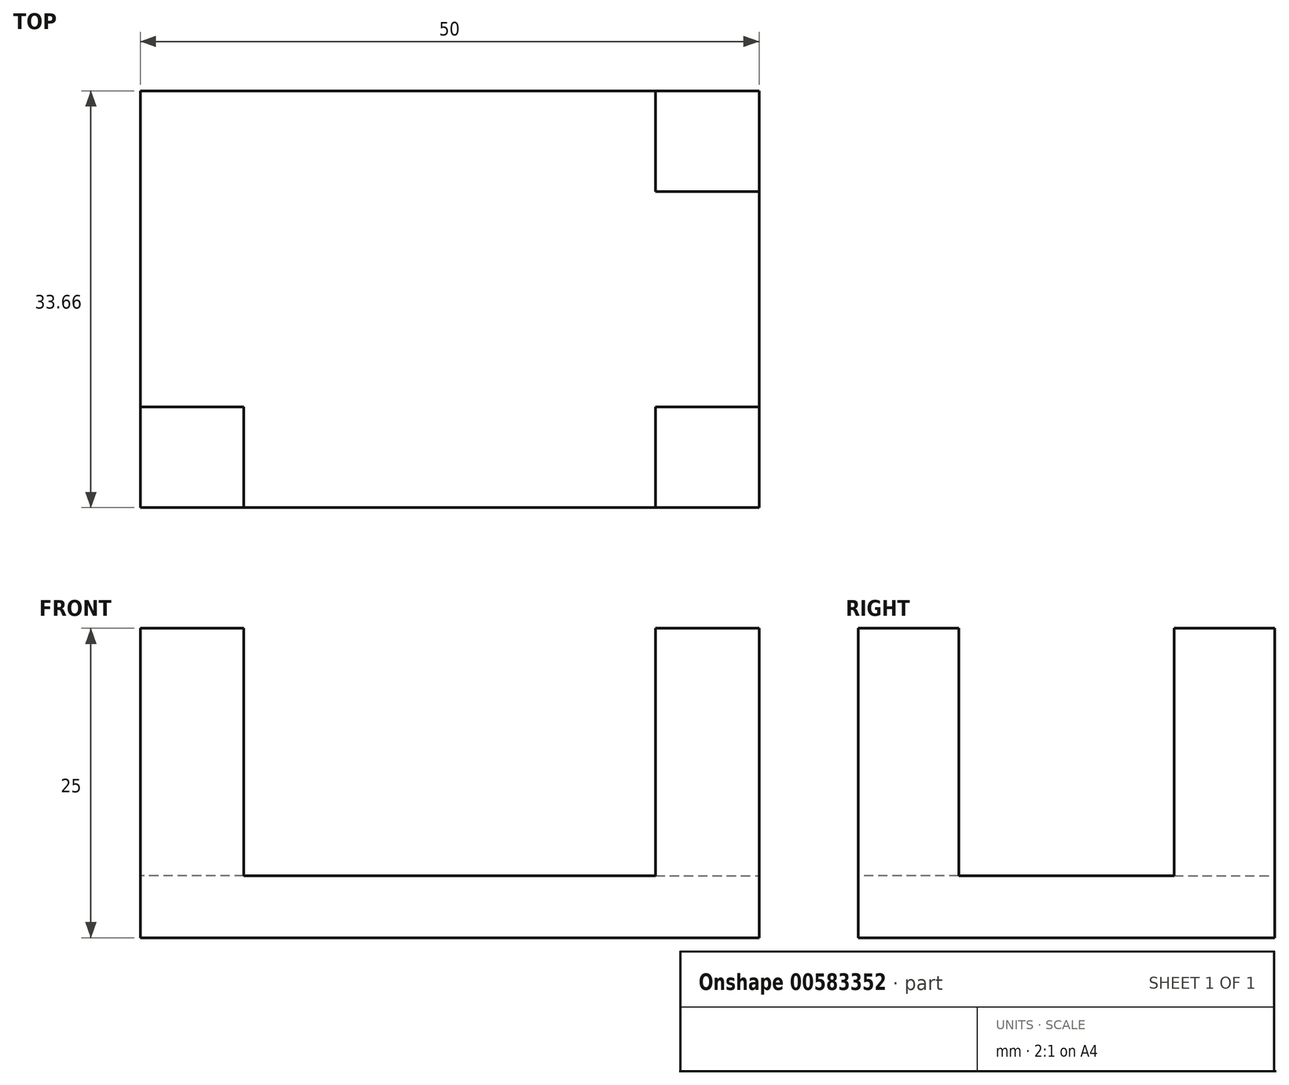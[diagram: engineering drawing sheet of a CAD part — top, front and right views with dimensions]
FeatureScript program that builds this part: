
annotation { "Feature Type Name" : "Feature", "Feature Type Description" : "" }
export const myFeature = defineFeature(function(context is Context, id is Id, definition is map)
    precondition{}
    {
        {
            var Q0;
            Q0=qCreatedBy(makeId("Top.planeOp"),FACE);
            var sketch = newSketch(context, id + "F0", { "sketchPlane" : qUnion([Q0])});
            skLineSegment(sketch, "E0.bottom", {"start": v(-25, 16.83) * mm, "end": v(25, 16.83) * mm});
            skLineSegment(sketch, "E0.top", {"start": v(-25, -16.83) * mm, "end": v(25, -16.83) * mm});
            skLineSegment(sketch, "E0.left", {"start": v(-25, 16.83) * mm, "end": v(-25, -16.83) * mm});
            skLineSegment(sketch, "E0.right", {"start": v(25, 16.83) * mm, "end": v(25, -16.83) * mm});
            skPoint(sketch, "E0.middle", {"position": v(0, 0) * mm});
            skLineSegment(sketch, "E1.bottom", {"start": v(-25, 16.83) * mm, "end": v(-16.63, 16.83) * mm});
            skLineSegment(sketch, "E1.top", {"start": v(-25, 8.7) * mm, "end": v(-16.63, 8.7) * mm});
            skLineSegment(sketch, "E1.left", {"start": v(-25, 16.83) * mm, "end": v(-25, 8.7) * mm});
            skLineSegment(sketch, "E1.right", {"start": v(-16.63, 16.83) * mm, "end": v(-16.63, 8.7) * mm});
            skLineSegment(sketch, "E2.MirrorCS", {"start": v(-25, -8.7) * mm, "end": v(-16.63, -8.7) * mm});
            skLineSegment(sketch, "E3.MirrorCS", {"start": v(-16.63, -16.83) * mm, "end": v(-16.63, -8.7) * mm});
            skLineSegment(sketch, "E4.MirrorCS", {"start": v(-25, -16.83) * mm, "end": v(-16.63, -16.83) * mm});
            skLineSegment(sketch, "E5.MirrorCS", {"start": v(-25, -16.83) * mm, "end": v(-25, -8.7) * mm});
            skLineSegment(sketch, "E6.MirrorCS", {"start": v(16.63, 16.83) * mm, "end": v(16.63, 8.7) * mm});
            skLineSegment(sketch, "E7.MirrorCS", {"start": v(25, 16.83) * mm, "end": v(16.63, 16.83) * mm});
            skLineSegment(sketch, "E8.MirrorCS", {"start": v(25, 16.83) * mm, "end": v(25, 8.7) * mm});
            skLineSegment(sketch, "E9.MirrorCS", {"start": v(25, 8.7) * mm, "end": v(16.63, 8.7) * mm});
            skLineSegment(sketch, "E10.MirrorCS", {"start": v(25, -8.7) * mm, "end": v(16.63, -8.7) * mm});
            skLineSegment(sketch, "E11.MirrorCS", {"start": v(25, -16.83) * mm, "end": v(25, -8.7) * mm});
            skLineSegment(sketch, "E12.MirrorCS", {"start": v(25, -16.83) * mm, "end": v(16.63, -16.83) * mm});
            skLineSegment(sketch, "E13.MirrorCS", {"start": v(16.63, -16.83) * mm, "end": v(16.63, -8.7) * mm});
            skSolve(sketch);
        }
        {
            var Q0;
            Q0=qSketchRegion(id+"F0",true);
            extrude(context, id + "F1", {"entities" : qUnion([Q0]), "depth" : 5 * mm, "offsetDistance" : 25 * mm});
        }
        {
            var Q0;
            Q0=makeQuery(id+"F0.imprint","IMPRINT",FACE,{"disambiguationData":[TD([[makeQuery(id+"F0.imprint","IMPRINT",EDGE,{"derivedFrom":sQuery(id+"F0.wireOp",EDGE,"E6.MirrorCS")}),1.0]])]});
            var Q1;
            Q1=makeQuery(id+"F0.imprint","IMPRINT",FACE,{"disambiguationData":[TD([[makeQuery(id+"F0.imprint","IMPRINT",EDGE,{"derivedFrom":sQuery(id+"F0.wireOp",EDGE,"E10.MirrorCS")}),1.0]])]});
            var Q2;
            Q2=makeQuery(id+"F0.imprint","IMPRINT",FACE,{"disambiguationData":[TD([[makeQuery(id+"F0.imprint","IMPRINT",EDGE,{"derivedFrom":sQuery(id+"F0.wireOp",EDGE,"E2.MirrorCS")}),-1.0]])]});
            var Q3;
            Q3=makeQuery(id+"F0.imprint","IMPRINT",FACE,{"disambiguationData":[TD([[makeQuery(id+"F0.imprint","IMPRINT",EDGE,{"derivedFrom":sQuery(id+"F0.wireOp",EDGE,"E1.bottom")}),-1.0]])]});
            extrude(context, id + "F2", {"entities" : qUnion([Q0, Q1, Q2, Q3]), "operationType" : NewBodyOperationType.ADD, "depth" : 25 * mm, "offsetDistance" : 25 * mm});
        }
    });
